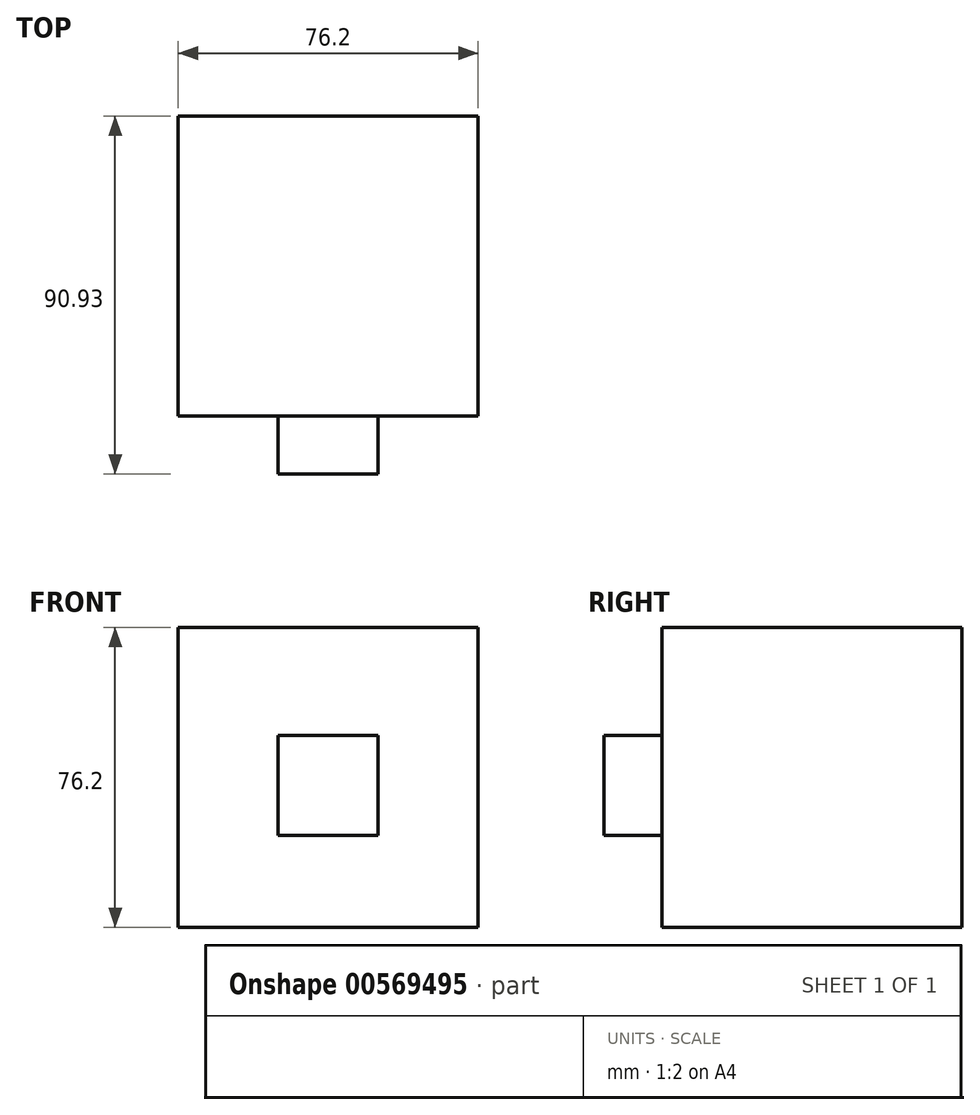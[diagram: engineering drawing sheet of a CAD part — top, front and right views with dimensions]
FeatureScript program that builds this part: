
annotation { "Feature Type Name" : "Feature", "Feature Type Description" : "" }
export const myFeature = defineFeature(function(context is Context, id is Id, definition is map)
    precondition{}
    {
        {
            var Q0;
            Q0=qCreatedBy(makeId("Front.planeOp"),FACE);
            var sketch = newSketch(context, id + "F0", { "sketchPlane" : qUnion([Q0])});
            skLineSegment(sketch, "E0.bottom", {"start": v(-76.2, 80.4) * mm, "end": v(0, 80.4) * mm});
            skLineSegment(sketch, "E0.top", {"start": v(-76.2, 4.2) * mm, "end": v(0, 4.2) * mm});
            skLineSegment(sketch, "E0.left", {"start": v(-76.2, 80.4) * mm, "end": v(-76.2, 4.2) * mm});
            skLineSegment(sketch, "E0.right", {"start": v(0, 80.4) * mm, "end": v(0, 4.2) * mm});
            skSolve(sketch);
        }
        {
            var Q0;
            Q0=makeQuery(id+"F0.imprint","IMPRINT",FACE,{"disambiguationData":[TD([[makeQuery(id+"F0.imprint","IMPRINT",EDGE,{"derivedFrom":sQuery(id+"F0.wireOp",EDGE,"E0.bottom")}),-1.0]])]});
            extrude(context, id + "F1", {"entities" : qUnion([Q0]), "depth" : 25.4 * mm, "offsetDistance" : 25.4 * mm});
        }
        {
            var Q0;
            Q0=makeQuery(id+"F0.imprint","IMPRINT",FACE,{"disambiguationData":[TD([[makeQuery(id+"F0.imprint","IMPRINT",EDGE,{"derivedFrom":sQuery(id+"F0.wireOp",EDGE,"E0.bottom")}),-1.0]])]});
            extrude(context, id + "F2", {"entities" : qUnion([Q0]), "operationType" : NewBodyOperationType.ADD, "depth" : 76.2 * mm, "offsetDistance" : 25.4 * mm});
        }
        {
            var Q0;
            Q0=makeQuery(id+"F2.opExtrude","CAP_FACE",FACE,{"disambiguationData":[OSD([sQuery(id+"F0.wireOp",EDGE,"E0.bottom"),sQuery(id+"F0.wireOp",EDGE,"E0.top"),sQuery(id+"F0.wireOp",EDGE,"E0.left"),sQuery(id+"F0.wireOp",EDGE,"E0.right")])],"isStart":false});
            var sketch = newSketch(context, id + "F3", { "sketchPlane" : qUnion([Q0])});
            skLineSegment(sketch, "E1.bottom", {"start": v(-50.8, 53.01) * mm, "end": v(-25.4, 53.01) * mm});
            skLineSegment(sketch, "E1.top", {"start": v(-50.8, 27.61) * mm, "end": v(-25.4, 27.61) * mm});
            skLineSegment(sketch, "E1.left", {"start": v(-50.8, 53.01) * mm, "end": v(-50.8, 27.61) * mm});
            skLineSegment(sketch, "E1.right", {"start": v(-25.4, 53.01) * mm, "end": v(-25.4, 27.61) * mm});
            skSolve(sketch);
        }
        {
            var Q0;
            Q0 = qSketchRegion(id + "F3", true);
            extrude(context, id + "F4", {"entities" : qUnion([Q0]), "operationType" : NewBodyOperationType.ADD, "depth" : 14.73 * mm, "offsetDistance" : 25.4 * mm});
        }
        {
            var Q0;
            {var subQ0=sQuery(id+"F0.wireOp",EDGE,"E0.right");Q0=makeQuery(id+"F2.boolean.opBoolean","MERGE",FACE,{"derivedFrom":[makeQuery(id+"F1.opExtrude","SWEPT_FACE",FACE,{"disambiguationData":[OSD([subQ0])]}),makeQuery(id+"F2.opExtrude","SWEPT_FACE",FACE,{"disambiguationData":[OSD([subQ0])]})]});}
            var sketch = newSketch(context, id + "F5", { "sketchPlane" : qUnion([Q0])});
            skCircle(sketch, "E2", {"center": v(-39.39, 42.3) * mm, "radius": 12.7 * mm});
            skSolve(sketch);
        }
        {
            var Q0;
            Q0=sQuery(id+"F5.wireOp",EDGE,"E2");
            extrude(context, id + "F6", {"bodyType" : ToolBodyType.SURFACE, "surfaceEntities" : qUnion([Q0]), "depth" : 10.4 * mm, "offsetDistance" : 25.4 * mm});
        }
    });
